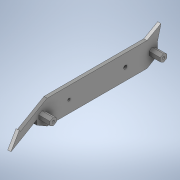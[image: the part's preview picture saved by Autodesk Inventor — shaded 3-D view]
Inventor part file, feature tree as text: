
AUTODESK INVENTOR PART (.ipt)
format: ipt  version: 2020 (Build 240168000, 168)  size: 179,200 bytes
history: native  units: in
note: dims shown in document units (in); Inventor stores cm internally (conversion verified against a paired STEP export)
features: other x3, extrude x2, sketch x2
ambient origin geometry x8: Origin, YZ Plane, XZ Plane, XY Plane, X Axis, Y Axis, Z Axis, Center Point
bodies: Solid1 (feature_tree)
feature tree (7):
  other  "HexWheelGuard.ipt"
  extrude  "Extrusion1"  TaperAngle=0.0deg  [1 undecoded]
  extrude  "Extrusion2"  Depth=0.3937in
  other  "Solid1::HexWheelGuard.ipt"
  other  "TaggingFeature1"
  sketch  "Sketch1"  dims[d0=0.3937in d6=0.0in d7=0.0in]
  sketch  "Sketch2"  dims[d9=0.315in d10=1.3858in d11=60.0deg d12=0.0787in d13=0.3937in d14=0.0in d20=0.3937in]
note: 1 required parameter value undecoded (feature->parameter linkage not recoverable at this tier; creation-order binding heuristic only, values carry confidence <= 0.55)
